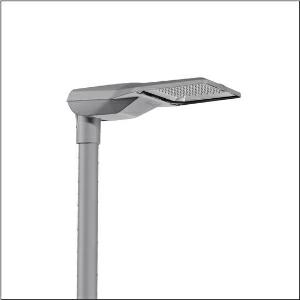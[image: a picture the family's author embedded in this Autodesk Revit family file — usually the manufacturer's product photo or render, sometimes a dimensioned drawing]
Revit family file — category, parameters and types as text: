
# Revit family: streetlight_sl_21_iq_midi___st1_0a_5xe3d61d08nb_4d1e
name_source: partatom
category: Lighting Fixtures
units: mm (PartAtom-declared; Revit-internal decimal feet)

## family parameters
Cut with Voids When Loaded = No
Host = Face
Light Source = No
Part Type = Normal
Room Calculation Point = No
Round Connector Dimension = Use Diameter
Shared = No

## types (1)
- --- (1 x LED, 20820 lm, 155.5 W, 2700K)
    Apparent Load = 155 VA
    CIE Flux Codes = 40 73 97 100 100
    Color Rendering = 70
    Color Temperature = 2700K
    Default Elevation = 1800 mm
    Description = Streetlight SL 21 iQ midi, mast luminaire, primary light control with lens, of PMMA, primary optical cover: cover, of toughened safety glass, transparent, light distribution: ST1.0a, light emission: direct distribution, primary light characteristic: asymmetric, installation type: post-top, side-entry, LED, High Power LED, rated luminous flux: 20.820lm, luminous efficacy: 134lm/W, light colour: 727, colour temperature: 2700K, control: Auto-Match, Temp-Guard, Lumen-Switch, Night-Set, Smart-Wire, Light-Fading, Desk-Remote (wireless, voltage-free reading and setting of iQ features in the workshop via application-optimized NFC function/RFID function), optimised constant luminous flux control (CLO 2.0), presetting dimming linear, mains connection: 230..240V, AC, 50/60Hz, start of lifetime: 156W, end of service life: 162W, reduction: 69W, luminaire housing, of diecast aluminium, powder-coated, Siteco® metallic grey (DB 702S), corrosivity category C5 mid according to DIN EN ISO 12944, please order mast flange separately, inclination adjustable: 0°, 5°, 10°, 15°, sealing non-destructively replaceable, multi-level sealing system, length: 644mm, width: 335mm, height: 110mm, mast flange for spigot size: 42mm (side-entry): 5XC10008XM4, 60/48mm (side-entry/post-top): 5XC10108XM2, 76/60mm (side-entry/post-top): 5XC10108XM1, protection rating (complete): IP66, insulation class (complete): insulation class II (safety insulation), certification: CE, ENEC, ENEC+, VDE, impact resistance: IK09, permissible operating ambient temperature for outdoor applications: -40..+50°C, standard-compliant lighting for roads and squares, packaging unit: 1 piece

Light Distribution: ST1.0a
    Height = 111 mm
    Lamp = 1 x LED
    Lamp Light Flux = 20820 lm
    Lamp Power = 155.5 W
    Lamp count = 1
    Length = 644 mm
    Luminous efficacy = 134 lm/W
    Manufacturer = Siteco
    ModVariant = No
    Model = 5XE3D61D08NB
    Number of Poles = 1
    OnlyDefault = Yes
    Power Factor = 1
    Product Name = Streetlight SL 21 iQ midi | ST1.0a
    Product group = mast luminaire | pylon top
    ProductGroupID = 6100
    Protection Class = Protection class II
    Protection Degree = IP 66
    RLX_Detail_Level = 1
    RLX_Emergency_Light_Flux = 0 lm
    RLX_Emergency_Type = 0
    RLX_Emergency_Type_DB = No
    RlxData = <blob elided: 90757 chars, md5=15926aad>
    Socket = socket
    Standby Power = 0 W
    System Light Flux = 20820 lm
    System Power = 155 W
    Type Comments = factory setting: luminous flux: 100 % | dim-lin: 254 | 823 mA
    Type Image = l_1004298.jpg
    URL = http://relux.com
    VarID = @adj_103463
    Voltage = 0 V
    Weight = 0.00 kg
    Width = 336 mm

## geometry (parser evidence)
native form markers: Blend x4, Sweep x10
no freeform markers — native parametric forms only
